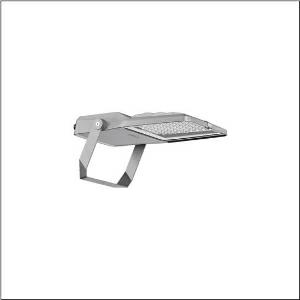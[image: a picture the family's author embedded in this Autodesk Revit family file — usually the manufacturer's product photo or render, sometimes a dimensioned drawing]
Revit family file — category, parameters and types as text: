
# Revit family: floodlight_fl_21_mini___pl61_5xa7776b2c1a_e1cc
name_source: partatom
category: Lighting Fixtures
units: mm (PartAtom-declared; Revit-internal decimal feet)

## family parameters
Cut with Voids When Loaded = No
Host = Face
Light Source = No
Part Type = Normal
Room Calculation Point = No
Round Connector Dimension = Use Diameter
Shared = No

## types (1)
- --- (1 x LED, 6110 lm, 45.7 W, 3000K)
    Apparent Load = 46 VA
    CIE Flux Codes = 33 65 98 100 100
    Color Rendering = 70
    Color Temperature = 3000K
    Default Elevation = 1800 mm
    Description = Floodlight FL 21 mini, floodlight, primary light control with lens, of PMMA, primary optical cover: protective disc, of toughened safety glass, transparent, light distribution: PL61, light emission: direct distribution, installation type: surface-mounted, LED, High Power LED, rated luminous flux: 6.110lm, luminous efficacy: 134lm/W, light colour: 730, colour temperature: 3000K, control gear: Smart Interface (Zhaga), control: flexible luminous flux parameterisation, time-dependent luminous flux control, constant luminous flux control, overheat protection, pre-setting: logarithmic dimming characteristic, with terminal, 6-pole, mains connection: 220..240V, AC, 50/60Hz, start of lifetime: 46W, end of service life: 48W, reduction: 22W, luminaire housing, of diecast aluminium, powder-coated, Siteco® metallic grey (DB 702S), corrosivity category C5 mid according to DIN EN ISO 12944, suitable for swimming pools, chlorine-resistant, sealing non-destructively replaceable, mounting bracket, of steel, galvanised, powder-coated, Siteco® metallic grey (DB 702S), Smart Interface below and above, protection rating (complete): IP66, insulation class (complete): insulation class II (safety insulation), certification: CE, ENEC, VDE, protection symbol: D, impact resistance: IK08, permissible operating ambient temperature: -40..+40°C, permissible operating ambient temperature for outdoor applications: -40..+50°C, standard: DIN EN 12944, LABS conformity tested according to VDMA 24364:2018-05, packaging unit: 1 piece

Light Distribution: PL61
    Height = 70 mm
    Lamp = 1 x LED
    Lamp Light Flux = 6110 lm
    Lamp Power = 45.7 W
    Lamp count = 1
    Length = 485 mm
    Luminous efficacy = 134 lm/W
    Manufacturer = Siteco
    ModVariant = No
    Model = 5XA7776B2C1A
    Number of Poles = 1
    OnlyDefault = Yes
    Power Factor = 1
    Product Name = Floodlight FL 21 mini | PL61
    Product group = floodlight | pylon annexe
    ProductGroupID = 6200
    Protection Class = Protection class II
    Protection Degree = IP 66
    RLX_Detail_Level = 1
    RLX_Emergency_Light_Flux = 0 lm
    RLX_Emergency_Type = 0
    RLX_Emergency_Type_DB = No
    RlxData = <blob elided: 96109 chars, md5=c9a4e0b7>
    Socket = socket
    Standby Power = 0 W
    System Light Flux = 6110 lm
    System Power = 46 W
    Type Comments = factory setting: luminous flux: 100 % | dim-lin: 254 | 463 mA
    Type Image = l_1006845.jpg
    URL = http://relux.com
    VarID = @adj_172160
    Voltage = 0 V
    Weight = 0.00 kg
    Width = 337 mm

## geometry (parser evidence)
native form markers: Blend x4, Sweep x12
no freeform markers — native parametric forms only
